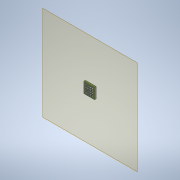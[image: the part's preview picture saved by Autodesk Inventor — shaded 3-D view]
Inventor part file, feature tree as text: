
AUTODESK INVENTOR PART (.ipt)
format: ipt  version: 2021 (Build 250183000, 183)  size: 241,152 bytes
history: native  units: in
note: dims shown in document units (in); Inventor stores cm internally (conversion verified against a paired STEP export)
features: extrude x3, sketch x3, pattern_linear x2, plane x1, mirror x1
ambient origin geometry x8: Origin, YZ Plane, XZ Plane, XY Plane, X Axis, Y Axis, Z Axis, Center Point
bodies: Solid1 (feature_tree)
feature tree (10):
  extrude  "Extrusion1"  Depth=0.25in
  extrude  "Extrusion2"  Depth=0.0394in
  extrude  "Extrusion3"  Depth=0.0006in
  plane  "Work Plane1"
  pattern_linear  "Rectangular Pattern3"  Spacing1=0.0in  [1 undecoded]
  pattern_linear  "Rectangular Pattern4"  Spacing1=0.0394in  [1 undecoded]
  mirror  "Mirror2"
  sketch  "Sketch1"  dims[d0=0.25in d1=0.25in]
  sketch  "Sketch2"  dims[d2=0.0394in d3=0.0in d4=0.0256in]
  sketch  "Sketch3"  dims[d5=0.05in d6=0.05in d7=0.0in d8=0.0in d15=0.0394in d16=0.0006in d17=0.0in d24=1.5748in d26=0.05in d27=1.5748in d29=0.05in d30=1.5748in d32=0.05in d33=1.5748in d35=0.05in]
note: 2 required parameter values undecoded (feature->parameter linkage not recoverable at this tier; creation-order binding heuristic only, values carry confidence <= 0.55)
